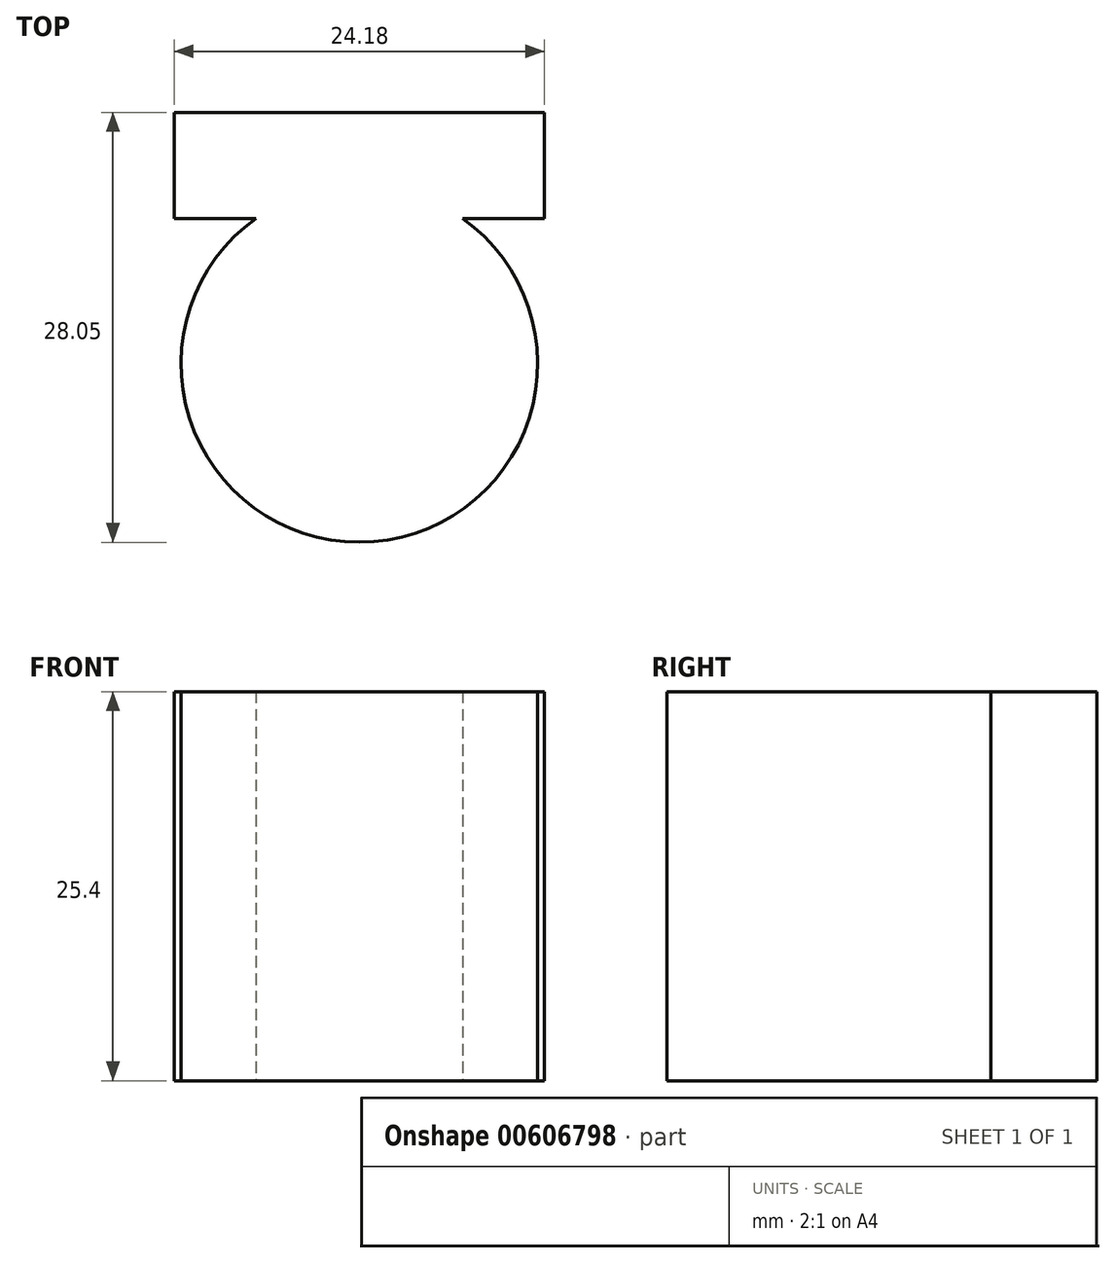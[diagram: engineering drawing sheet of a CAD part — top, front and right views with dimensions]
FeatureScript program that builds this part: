
annotation { "Feature Type Name" : "Feature", "Feature Type Description" : "" }
export const myFeature = defineFeature(function(context is Context, id is Id, definition is map)
    precondition{}
    {
        {
            var Q0;
            Q0=qCreatedBy(makeId("Top.planeOp"),FACE);
            var sketch = newSketch(context, id + "F0", { "sketchPlane" : qUnion([Q0])});
            skCircle(sketch, "E0", {"center": v(-36.12, 22.3) * mm, "radius": 11.64 * mm});
            skLineSegment(sketch, "E1.bottom", {"start": v(-48.2, 38.7) * mm, "end": v(-24.03, 38.7) * mm});
            skLineSegment(sketch, "E1.top", {"start": v(-48.2, 31.8) * mm, "end": v(-24.03, 31.8) * mm});
            skLineSegment(sketch, "E1.left", {"start": v(-48.2, 38.7) * mm, "end": v(-48.2, 31.8) * mm});
            skLineSegment(sketch, "E1.right", {"start": v(-24.03, 38.7) * mm, "end": v(-24.03, 31.8) * mm});
            skSolve(sketch);
        }
        {
            var Q0;
            Q0 = qSketchRegion(id + "F0", true);
            extrude(context, id + "F1", {"entities" : qUnion([Q0]), "depth" : 25.4 * mm, "offsetDistance" : 25.4 * mm});
        }
    });
